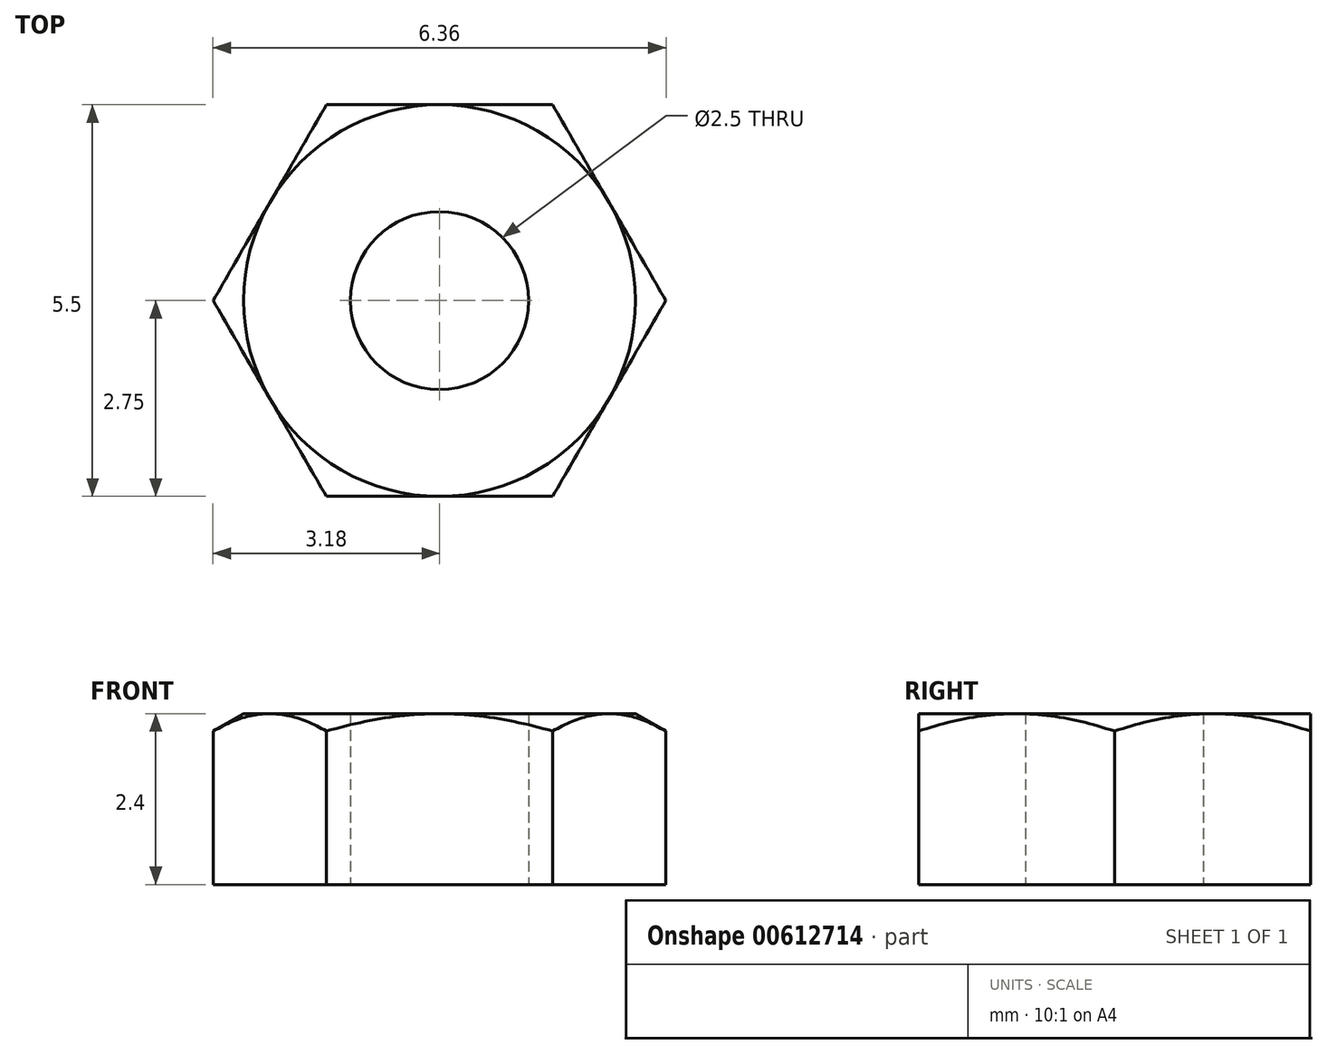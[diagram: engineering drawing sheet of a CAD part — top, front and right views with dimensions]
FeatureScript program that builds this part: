
annotation { "Feature Type Name" : "Feature", "Feature Type Description" : "" }
export const myFeature = defineFeature(function(context is Context, id is Id, definition is map)
    precondition{}
    {
        {
            var Q0;
            Q0=qCreatedBy(makeId("Top.planeOp"),FACE);
            var sketch = newSketch(context, id + "F0", { "sketchPlane" : qUnion([Q0])});
            skCircle(sketch, "E0", {"center": v(0, 0) * mm, "radius": 1.25 * mm});
            skCircle(sketch, "E1.cCircle", {"center": v(0, 0) * mm, "radius": 2.75 * mm, "construction": true});
            skLineSegment(sketch, "E1.0", {"start": v(1.59, 2.75) * mm, "end": v(3.18, 0) * mm});
            skLineSegment(sketch, "E1.1", {"start": v(3.18, 0) * mm, "end": v(1.59, -2.75) * mm});
            skLineSegment(sketch, "E1.2", {"start": v(1.59, -2.75) * mm, "end": v(-1.59, -2.75) * mm});
            skLineSegment(sketch, "E1.3", {"start": v(-1.59, -2.75) * mm, "end": v(-3.18, 0) * mm});
            skLineSegment(sketch, "E1.4", {"start": v(-3.18, 0) * mm, "end": v(-1.59, 2.75) * mm});
            skLineSegment(sketch, "E1.5", {"start": v(-1.59, 2.75) * mm, "end": v(1.59, 2.75) * mm});
            skPoint(sketch, "E1.0.midPoint", {"position": v(2.38, 1.37) * mm});
            skSolve(sketch);
        }
        {
            var Q0;
            Q0=makeQuery(id+"F0.imprint","IMPRINT",FACE,{"disambiguationData":[TD([[makeQuery(id+"F0.imprint","IMPRINT",EDGE,{"derivedFrom":sQuery(id+"F0.wireOp",EDGE,"E0")}),-1.0]])]});
            extrude(context, id + "F1", {"entities" : qUnion([Q0]), "endBound" : BoundingType.SYMMETRIC, "depth" : 3 * 0.8 * mm, "offsetDistance" : 25 * mm});
        }
        {
            var Q0;
            Q0=qCreatedBy(makeId("Front.planeOp"),FACE);
            var sketch = newSketch(context, id + "F2", { "sketchPlane" : qUnion([Q0])});
            skLineSegment(sketch, "E2", {"start": v(2.75, 1.2) * mm, "end": v(3.18, 1.2) * mm});
            skLineSegment(sketch, "E3", {"start": v(3.18, 1.2) * mm, "end": v(3.18, 0.95) * mm});
            skLineSegment(sketch, "E4", {"start": v(3.18, 0.95) * mm, "end": v(2.75, 1.2) * mm});
            skLineSegment(sketch, "E5", {"start": v(0, 0) * mm, "end": v(0, 2.72) * mm, "construction": true});
            skSolve(sketch);
        }
        {
            var Q0;
            Q0=qSketchRegion(id+"F2",true);
            var Q1;
            Q1=sQuery(id+"F2.wireOp",EDGE,"E5");
            revolve(context, id + "F3", {"operationType" : NewBodyOperationType.REMOVE, "surfaceOperationType" : NewSurfaceOperationType.NEW, "entities" : qUnion([Q0]), "axis" : qUnion([Q1]), "revolveType" : RevolveType.FULL, "oppositeDirection" : true});
        }
    });
